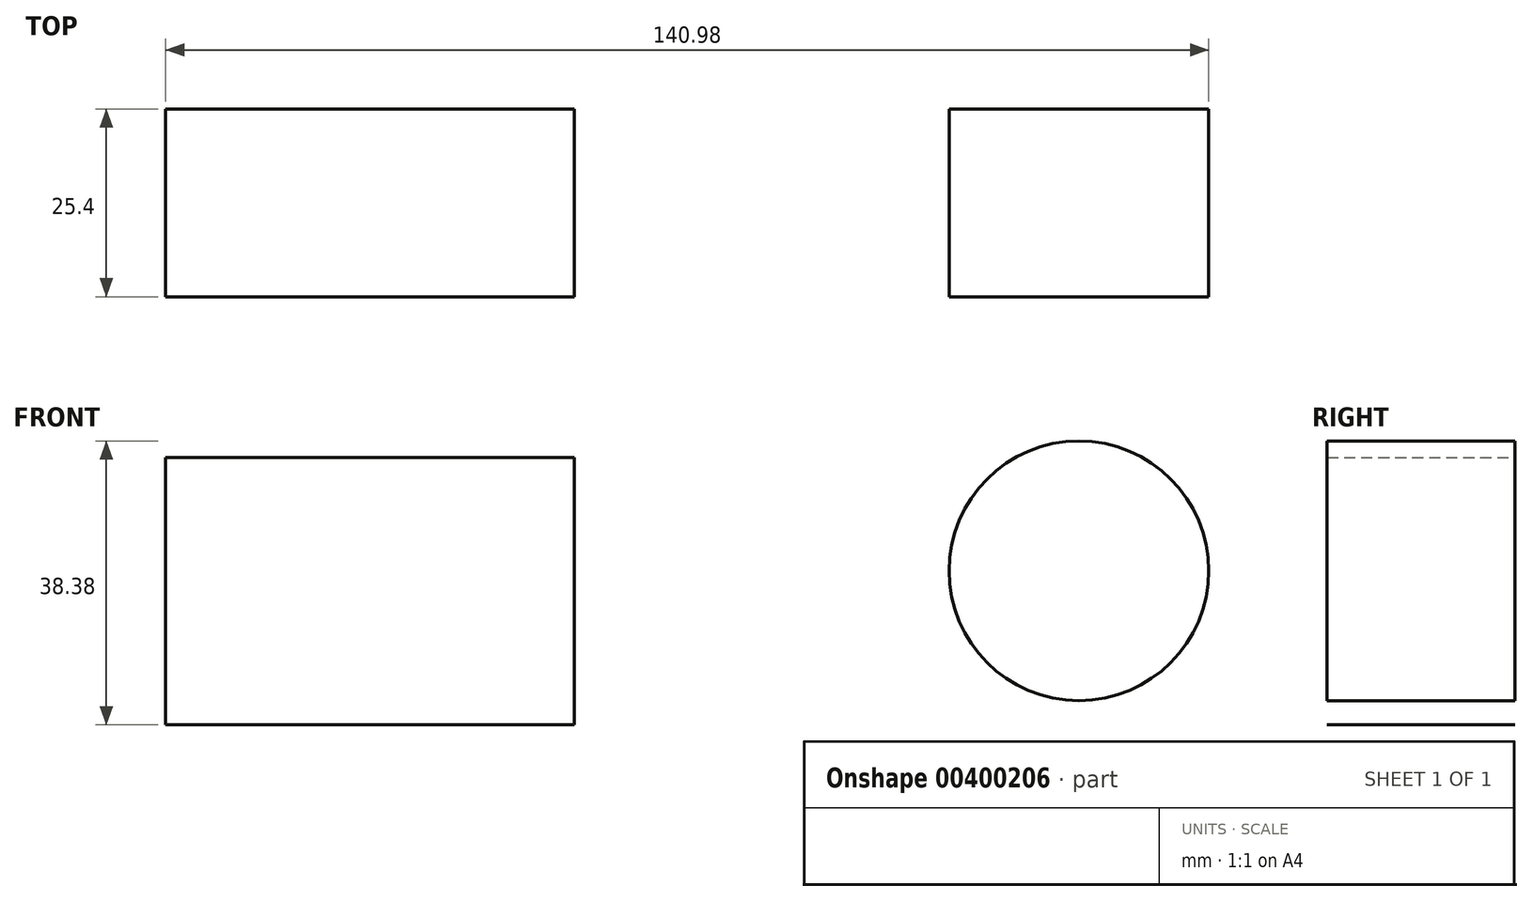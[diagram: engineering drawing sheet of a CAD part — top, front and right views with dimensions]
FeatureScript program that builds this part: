
annotation { "Feature Type Name" : "Feature", "Feature Type Description" : "" }
export const myFeature = defineFeature(function(context is Context, id is Id, definition is map)
    precondition{}
    {
        {
            var Q0;
            Q0=qCreatedBy(makeId("Front.planeOp"),FACE);
            var sketch = newSketch(context, id + "F0", { "sketchPlane" : qUnion([Q0])});
            skLineSegment(sketch, "E0.bottom", {"start": v(-85.94, 48.2) * mm, "end": v(-30.7, 48.2) * mm});
            skLineSegment(sketch, "E0.top", {"start": v(-85.94, 12.02) * mm, "end": v(-30.7, 12.02) * mm});
            skLineSegment(sketch, "E0.left", {"start": v(-85.94, 48.2) * mm, "end": v(-85.94, 12.02) * mm});
            skLineSegment(sketch, "E0.right", {"start": v(-30.7, 48.2) * mm, "end": v(-30.7, 12.02) * mm});
            skCircle(sketch, "E1", {"center": v(37.5, 32.85) * mm, "radius": 17.55 * mm});
            skSolve(sketch);
        }
        {
            var Q0;
            Q0 = qSketchRegion(id + "F0", true);
            extrude(context, id + "F1", {"entities" : qUnion([Q0]), "depth" : 25.4 * mm});
        }
    });
